# Revit family: HVAC_Ortal_Fireplace_Wilderness_Traditional2
name_source: partatom
category: Specialty Equipment
units: mm (PartAtom-declared; Revit-internal decimal feet)

## family parameters
Cut with Voids When Loaded = Yes
Host = Face
OmniClass Number = 23.40.20.34.14
OmniClass Title = Fireplaces
Part Type = Normal
Room Calculation Point = No
Round Connector Dimension = Use Diameter
Shared = No

## types (4) — shared parameters
Apparent Load = 750 VA
Assembly Code = E1090400
Certification = ANSI Z21.88/CSA 2.33-2019
Current = 15 A
Default Elevation = 0"
Depth = 27 1/2"
Description = Wilderness Type Traditional Fireplace
Edition number = 1
Frequency = 60 Hz
Gas Flow = 0 GPM
Gas Inlet Diameter = 1/2"
Gas Type = Gas : Natural Gas
Keynote = 15500
Manufacturer = Ortal
Number of Poles = 3
Power Factor = 0.8
Product Material = Ortal - Stainless Steel - Black
Product data url = https://www.bimobject.com
Total Heating Capacity = 32163.0 Btu/h
URL = https://www.ortalheat.com
Vent = 5x8 co-axial direct vent pipe (5” interior, 8” exterior)
Voltage = 120 V
z_Frame Thickness = 3/16"
z_Gas Type 1 = Gas : Natural Gas
z_Gas Type 2 = Gas : Propane
z_Glass Depth = 2 1/2"
z_HB Depth = 1"
z_Vent Depth = 18 1/16"

## per-type parameters (varying)
| type | Efficiency | Height | Product Guid | Viewing Area Height | Viewing Area Width | Weight | Width | z_36" | z_42" | z_Back Leg Offset | z_Bottom | z_Double Glass | z_Front Leg Offset | z_Screen | z_Top |
| Wilderness Traditional 36" - Double Glass | 79.7% | 51 3/4" | 41f85e15-86c4-4da1-b3b9-b7d5860bb208 | 31 5/8" | 35 7/16" | 306.00 lbf | 45 13/16" | Yes | No | 11 1/16" | 9 13/16" | Yes | 5 3/8" | No | 6" |
| Wilderness Traditional 36" - Screen | 79.7% | 43 5/8" | 41f85e15-86c4-4da1-b3b9-b7d5860bb208 | 31 5/8" | 35 7/16" | 306.00 lbf | 45 13/16" | Yes | No | 11 1/16" | 1 5/8" | No | 5 3/8" | Yes | 6" |
| Wilderness Traditional 42" - Double Glass | 81.4% | 54 1/4" | 7d60c6c6-2028-4fca-8733-d36870c23f6c | 34 1/8" | 42 11/16" | 357.00 lbf | 53 5/16" | No | Yes | 14 3/8" | 9 13/16" | Yes | 4 5/8" | No | 5 1/2" |
| Wilderness Traditional 42" - Screen | 81.4% | 46 1/8" | 7d60c6c6-2028-4fca-8733-d36870c23f6c | 34 1/8" | 42 11/16" | 337.00 lbf | 53 5/16" | No | Yes | 14 3/8" | 1 5/8" | No | 4 5/8" | Yes | 5 1/2" |

note: column(s) folded — value = type name in every type: Model

## geometry (parser evidence)
native form markers: Sweep x4
no freeform markers — native parametric forms only
